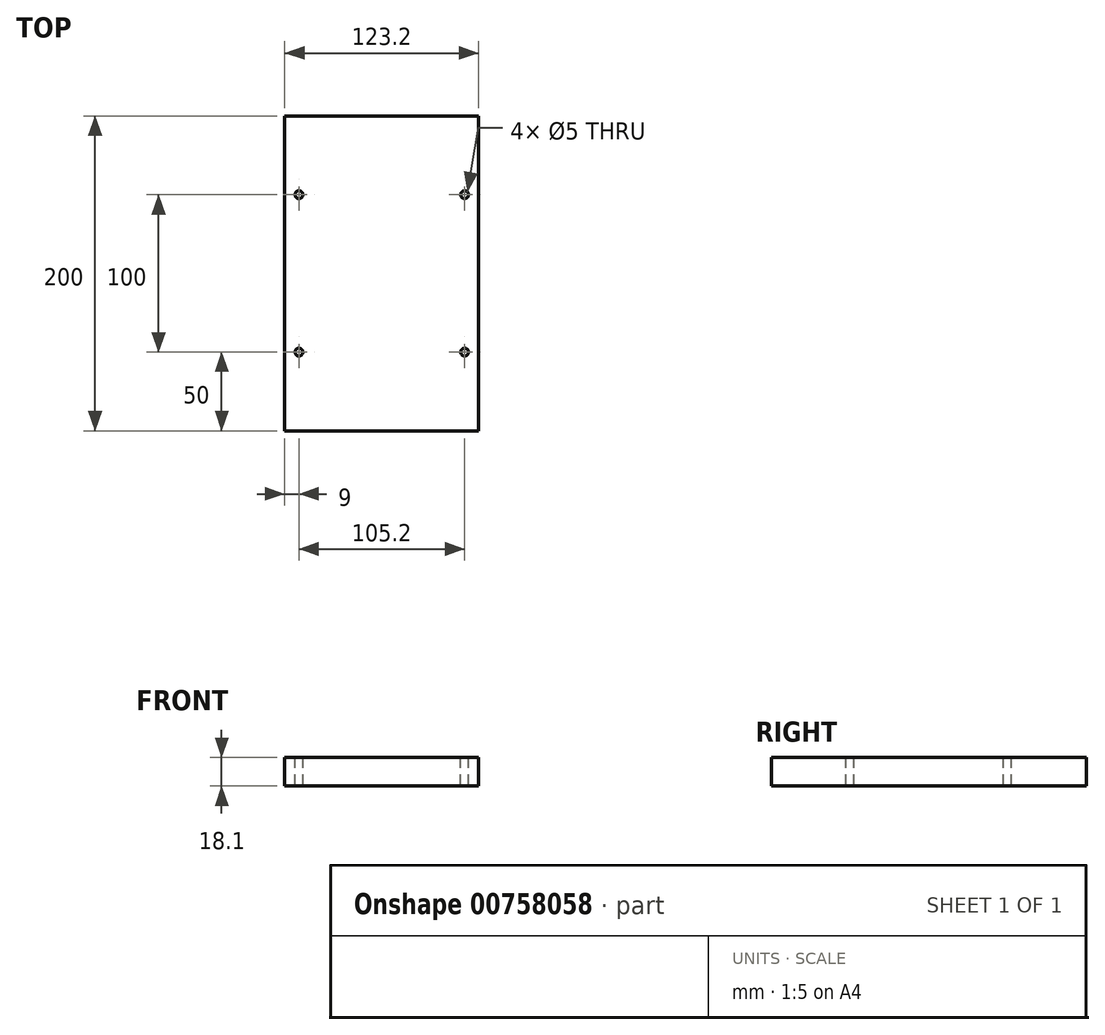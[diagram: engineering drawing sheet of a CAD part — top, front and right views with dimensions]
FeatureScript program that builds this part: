
annotation { "Feature Type Name" : "Feature", "Feature Type Description" : "" }
export const myFeature = defineFeature(function(context is Context, id is Id, definition is map)
    precondition{}
    {
        {
            var Q0;
            Q0=qCreatedBy(makeId("Top.planeOp"),FACE);
            var sketch = newSketch(context, id + "F0", { "sketchPlane" : qUnion([Q0])});
            skLineSegment(sketch, "E0.bottom", {"start": v(-61.6, 100) * mm, "end": v(61.6, 100) * mm});
            skLineSegment(sketch, "E0.top", {"start": v(-61.6, -100) * mm, "end": v(61.6, -100) * mm});
            skLineSegment(sketch, "E0.left", {"start": v(-61.6, 100) * mm, "end": v(-61.6, -100) * mm});
            skLineSegment(sketch, "E0.right", {"start": v(61.6, 100) * mm, "end": v(61.6, -100) * mm});
            skPoint(sketch, "E0.middle", {"position": v(0, 0) * mm});
            skSolve(sketch);
        }
        {
            var Q0;
            Q0=makeQuery(id+"F0.imprint","IMPRINT",FACE,{"disambiguationData":[TD([[makeQuery(id+"F0.imprint","IMPRINT",EDGE,{"derivedFrom":sQuery(id+"F0.wireOp",EDGE,"E0.bottom")}),-1.0]])]});
            extrude(context, id + "F1", {"entities" : qUnion([Q0]), "depth" : 18.1 * mm, "offsetDistance" : 25 * mm});
        }
        {
            var Q0;
            Q0=makeQuery(id+"F1.opExtrude","CAP_FACE",FACE,{"disambiguationData":[OSD([sQuery(id+"F0.wireOp",EDGE,"E0.bottom"),sQuery(id+"F0.wireOp",EDGE,"E0.top"),sQuery(id+"F0.wireOp",EDGE,"E0.left"),sQuery(id+"F0.wireOp",EDGE,"E0.right")])],"isStart":false});
            var sketch = newSketch(context, id + "F2", { "sketchPlane" : qUnion([Q0])});
            skLineSegment(sketch, "E1", {"start": v(52.6, 37.85) * mm, "end": v(52.6, -37.41) * mm, "construction": true});
            skLineSegment(sketch, "E2", {"start": v(0, 0) * mm, "end": v(0, 19.11) * mm, "construction": true});
            skCircle(sketch, "E3", {"center": v(52.6, 50) * mm, "radius": 2.5 * mm});
            skCircle(sketch, "E4", {"center": v(52.6, -50) * mm, "radius": 2.5 * mm});
            skCircle(sketch, "E5.MirrorC", {"center": v(-52.6, -50) * mm, "radius": 2.5 * mm});
            skLineSegment(sketch, "E6.MirrorCS", {"start": v(-52.6, 37.85) * mm, "end": v(-52.6, -37.41) * mm, "construction": true});
            skCircle(sketch, "E7.MirrorC", {"center": v(-52.6, 50) * mm, "radius": 2.5 * mm});
            skSolve(sketch);
        }
        {
            var Q0;
            Q0 = qSketchRegion(id + "F2", true);
            extrude(context, id + "F3", {"entities" : qUnion([Q0]), "operationType" : NewBodyOperationType.REMOVE, "oppositeDirection" : true, "depth" : 25 * mm, "offsetDistance" : 25 * mm});
        }
    });
